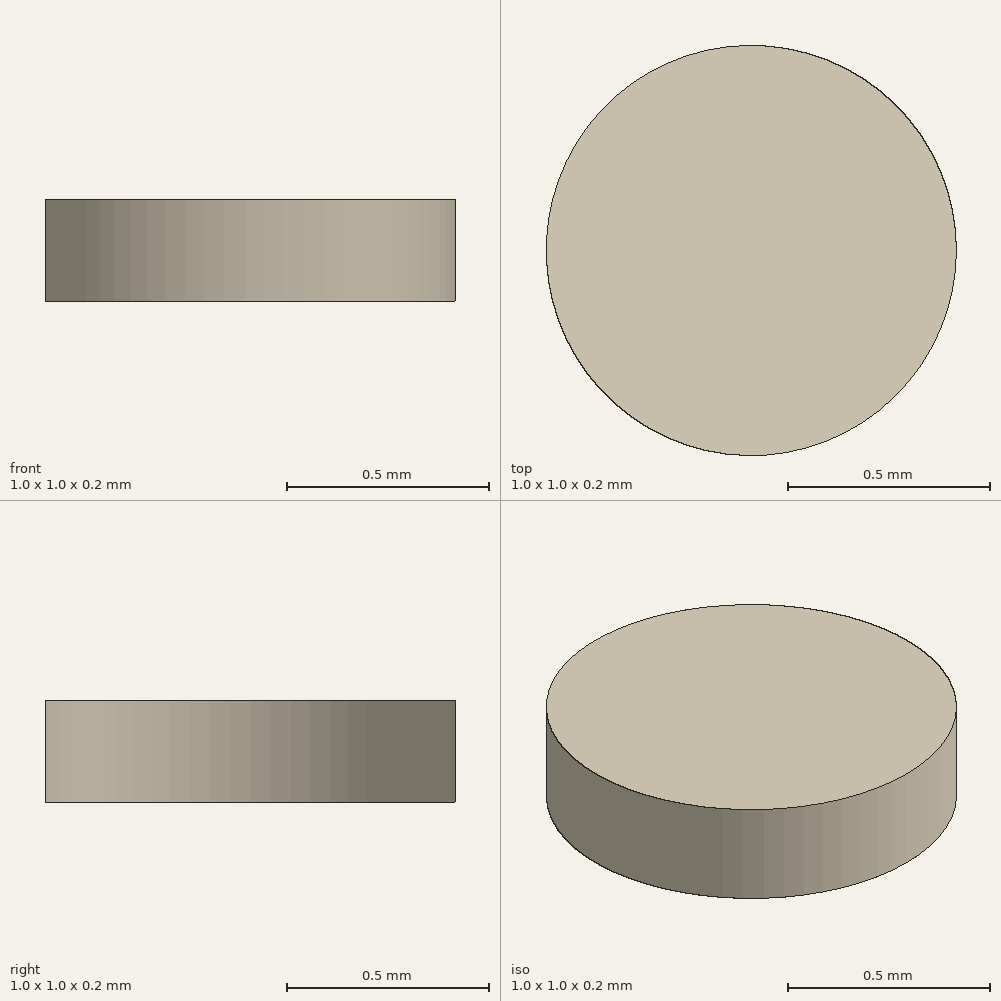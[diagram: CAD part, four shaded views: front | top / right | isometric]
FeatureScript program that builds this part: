
annotation { "Feature Type Name" : "Feature", "Feature Type Description" : "" }
export const myFeature = defineFeature(function(context is Context, id is Id, definition is map)
    precondition{}
    {
        {
            var Q0;
            Q0=qCreatedBy(makeId("Top.planeOp"),FACE);
            var sketch = newSketch(context, id + "F0", { "sketchPlane" : qUnion([Q0])});
            skCircle(sketch, "E0", {"center": v(25.16, 28.56) * mm, "radius": 0.5 * mm});
            skSolve(sketch);
        }
        {
            var Q0;
            Q0 = qSketchRegion(id + "F0", true);
            extrude(context, id + "F1", {"entities" : qUnion([Q0]), "depth" : 0.25 * mm});
        }
    });
